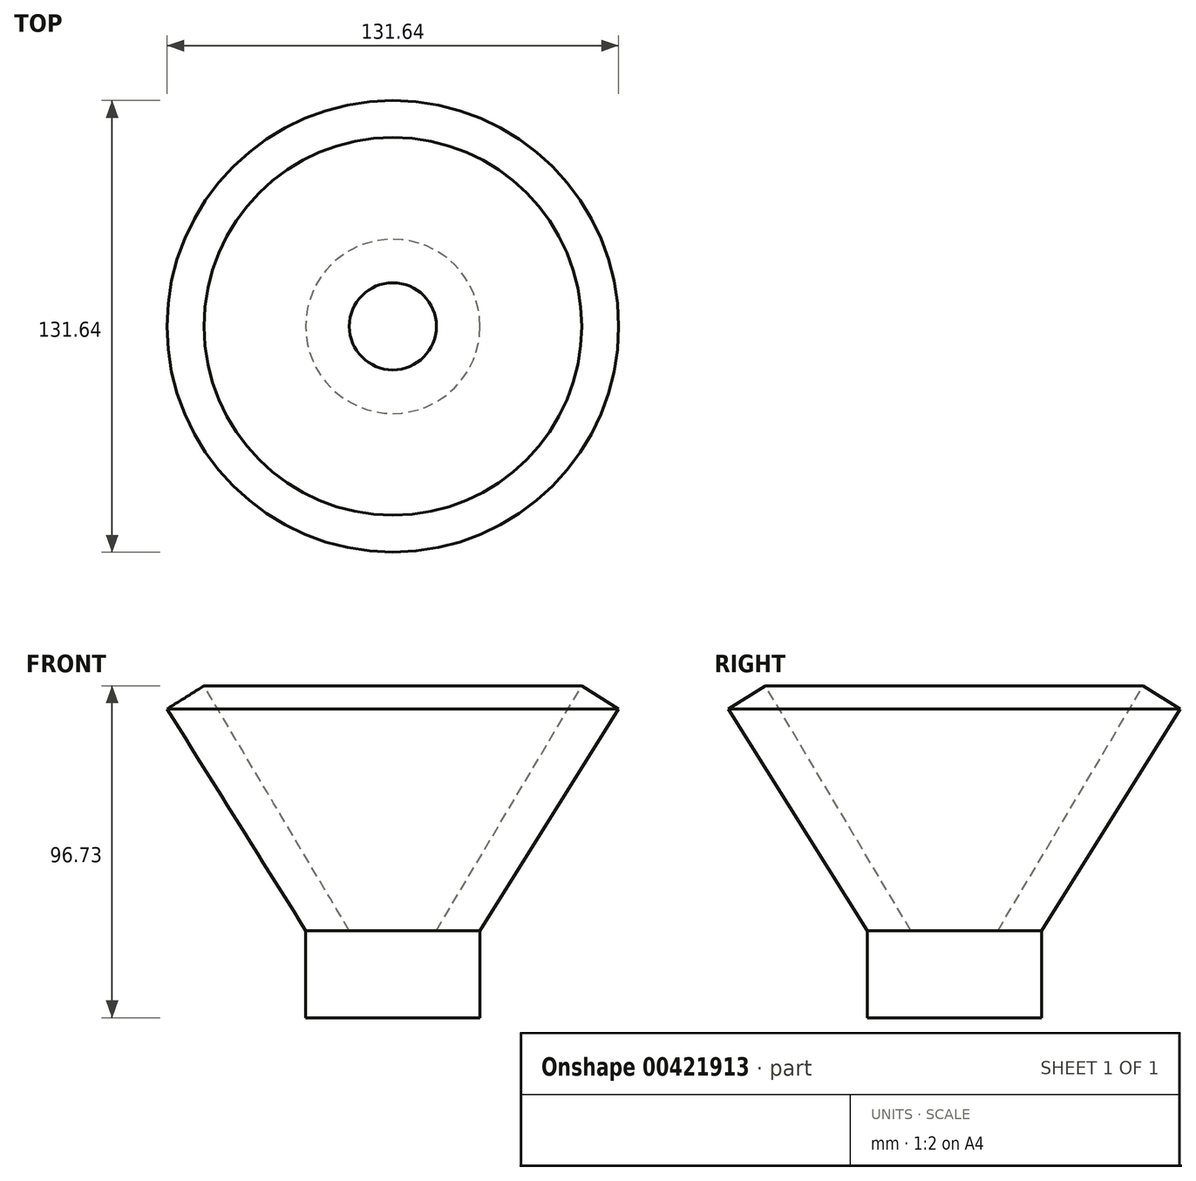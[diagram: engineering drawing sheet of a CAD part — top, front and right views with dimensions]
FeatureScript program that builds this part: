
annotation { "Feature Type Name" : "Feature", "Feature Type Description" : "" }
export const myFeature = defineFeature(function(context is Context, id is Id, definition is map)
    precondition{}
    {
        {
            var Q0;
            Q0=qCreatedBy(makeId("Front.planeOp"),FACE);
            var sketch = newSketch(context, id + "F0", { "sketchPlane" : qUnion([Q0])});
            skLineSegment(sketch, "E0", {"start": v(-25.4, -25.4) * mm, "end": v(0, -25.4) * mm});
            skLineSegment(sketch, "E1", {"start": v(0, -25.4) * mm, "end": v(0, 0) * mm});
            skLineSegment(sketch, "E2", {"start": v(0, 0) * mm, "end": v(40.42, 64.6) * mm});
            skLineSegment(sketch, "E3", {"start": v(-25.4, -25.4) * mm, "end": v(-25.4, 0) * mm});
            skLineSegment(sketch, "E4", {"start": v(40.42, 64.6) * mm, "end": v(29.65, 71.33) * mm});
            skLineSegment(sketch, "E5", {"start": v(-25.4, 0) * mm, "end": v(-12.7, 0) * mm});
            skLineSegment(sketch, "E6", {"start": v(-12.7, 0) * mm, "end": v(29.65, 71.33) * mm});
            skSolve(sketch);
        }
        {
            var Q0;
            Q0=makeQuery(id+"F0.imprint","IMPRINT",FACE,{"disambiguationData":[TD([[makeQuery(id+"F0.imprint","IMPRINT",EDGE,{"derivedFrom":sQuery(id+"F0.wireOp",EDGE,"E0")}),1.0]])]});
            var Q1;
            Q1=sQuery(id+"F0.wireOp",EDGE,"E3");
            revolve(context, id + "F1", {"entities" : qUnion([Q0]), "axis" : qUnion([Q1]), "revolveType" : RevolveType.FULL});
        }
    });
